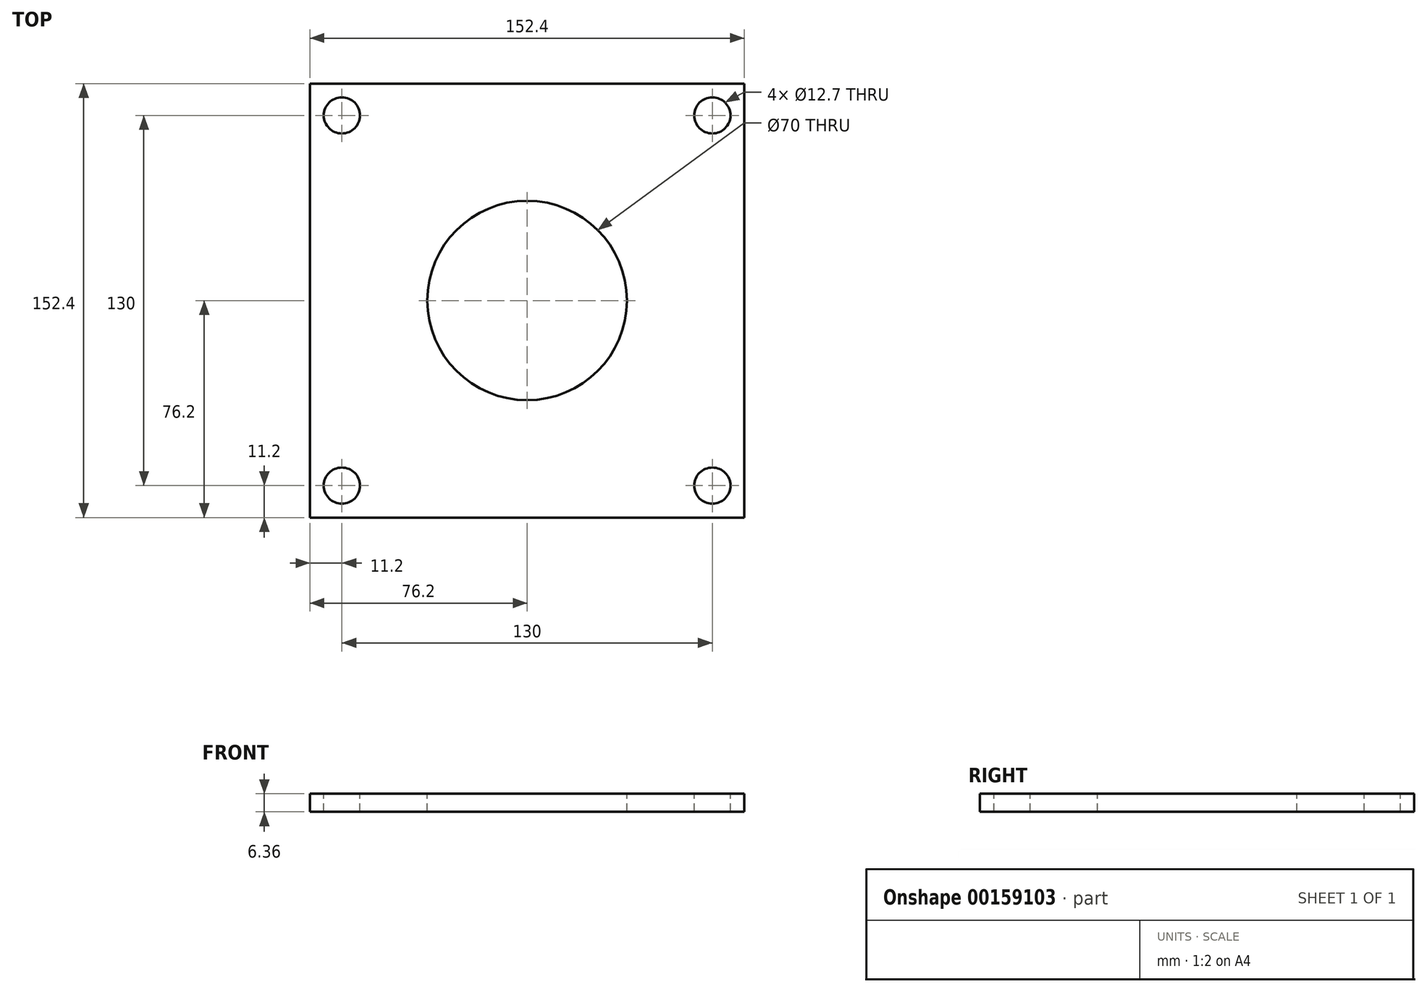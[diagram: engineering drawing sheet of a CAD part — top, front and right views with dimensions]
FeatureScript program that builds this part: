
annotation { "Feature Type Name" : "Feature", "Feature Type Description" : "" }
export const myFeature = defineFeature(function(context is Context, id is Id, definition is map)
    precondition{}
    {
        {
            var Q0;
            Q0=qCreatedBy(makeId("Top.planeOp"),FACE);
            var sketch = newSketch(context, id + "F0", { "sketchPlane" : qUnion([Q0])});
            skLineSegment(sketch, "E0.bottom", {"start": v(-76.2, 76.2) * mm, "end": v(76.2, 76.2) * mm});
            skLineSegment(sketch, "E0.top", {"start": v(-76.2, -76.2) * mm, "end": v(76.2, -76.2) * mm});
            skLineSegment(sketch, "E0.left", {"start": v(-76.2, 76.2) * mm, "end": v(-76.2, -76.2) * mm});
            skLineSegment(sketch, "E0.right", {"start": v(76.2, 76.2) * mm, "end": v(76.2, -76.2) * mm});
            skLineSegment(sketch, "E1.bottom", {"start": v(-65, 65) * mm, "end": v(65, 65) * mm, "construction": true});
            skLineSegment(sketch, "E1.top", {"start": v(-65, -65) * mm, "end": v(65, -65) * mm, "construction": true});
            skLineSegment(sketch, "E1.left", {"start": v(-65, 65) * mm, "end": v(-65, -65) * mm, "construction": true});
            skLineSegment(sketch, "E1.right", {"start": v(65, 65) * mm, "end": v(65, -65) * mm, "construction": true});
            skCircle(sketch, "E2", {"center": v(-65, 65) * mm, "radius": 6.35 * mm});
            skCircle(sketch, "E3.MirrorC", {"center": v(65, 65) * mm, "radius": 6.35 * mm});
            skCircle(sketch, "E4.MirrorC", {"center": v(-65, -65) * mm, "radius": 6.35 * mm});
            skCircle(sketch, "E5.MirrorC", {"center": v(65, -65) * mm, "radius": 6.35 * mm});
            skCircle(sketch, "E6", {"center": v(0, 0) * mm, "radius": 35 * mm});
            skCircle(sketch, "E7", {"center": v(0, 5.24) * mm, "radius": 2.62 * mm, "construction": true});
            skCircle(sketch, "E8.1.0", {"center": v(-4.54, -2.62) * mm, "radius": 2.62 * mm, "construction": true});
            skCircle(sketch, "E8.2.0", {"center": v(4.54, -2.62) * mm, "radius": 2.62 * mm, "construction": true});
            skCircle(sketch, "E9", {"center": v(0, 0) * mm, "radius": 8.01 * mm, "construction": true});
            skCircle(sketch, "E10", {"center": v(0, 0) * mm, "radius": 10.01 * mm, "construction": true});
            skSolve(sketch);
        }
        {
            var Q0;
            Q0=makeQuery(id+"F0.imprint","IMPRINT",FACE,{"disambiguationData":[TD([[makeQuery(id+"F0.imprint","IMPRINT",EDGE,{"derivedFrom":sQuery(id+"F0.wireOp",EDGE,"E0.bottom")}),-1.0]])]});
            extrude(context, id + "F1", {"entities" : qUnion([Q0]), "endBound" : BoundingType.SYMMETRIC, "oppositeDirection" : true, "depth" : 6.35 * mm});
        }
    });
